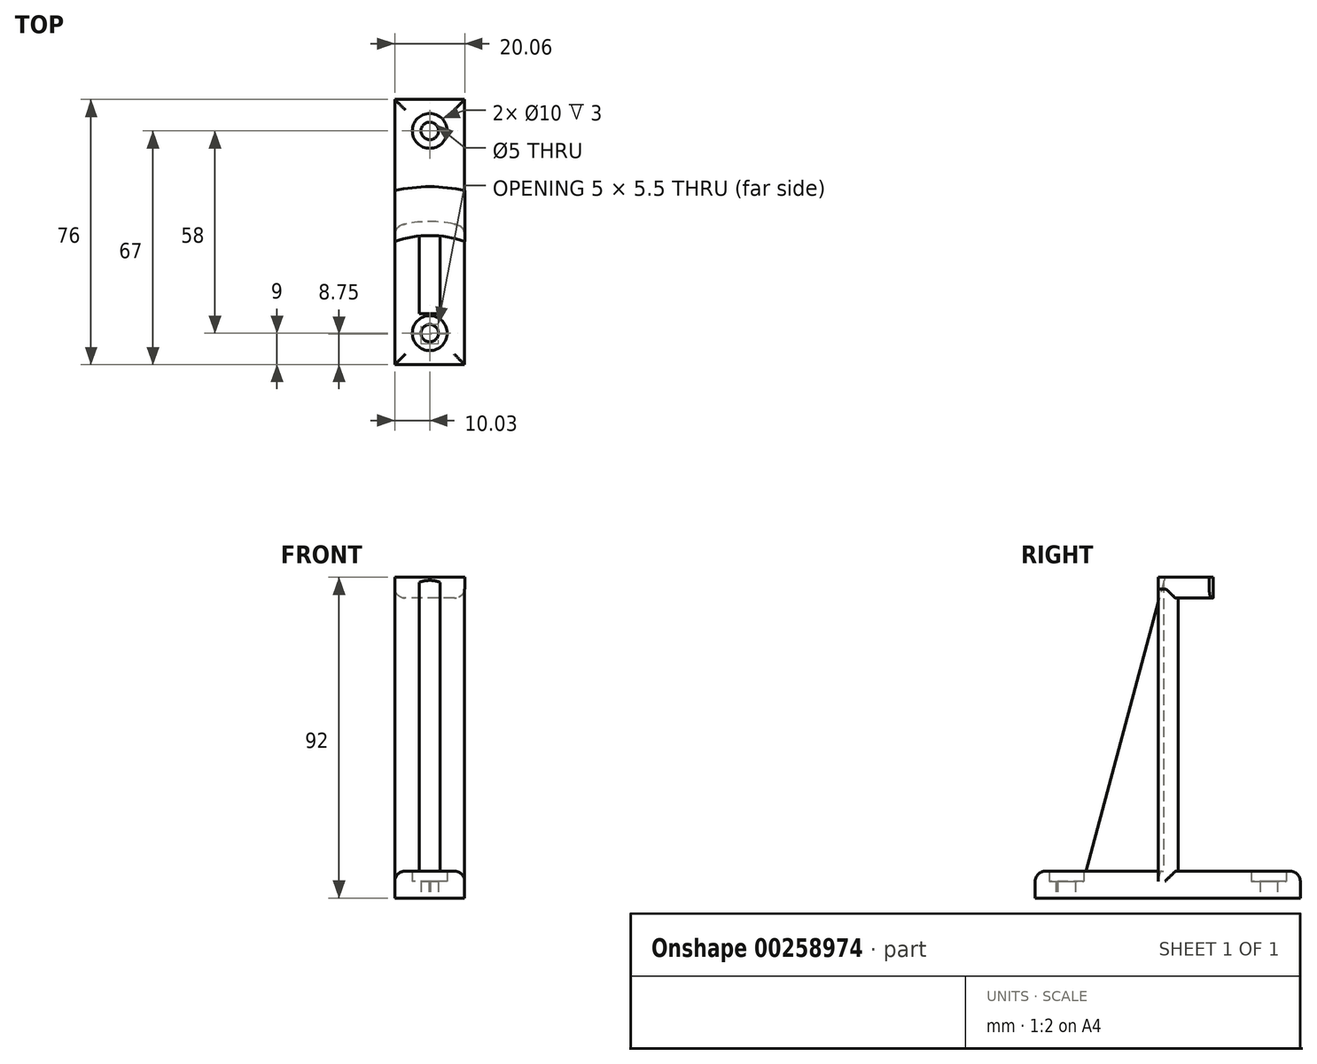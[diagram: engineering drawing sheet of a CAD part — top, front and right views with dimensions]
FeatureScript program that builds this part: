
annotation { "Feature Type Name" : "Feature", "Feature Type Description" : "" }
export const myFeature = defineFeature(function(context is Context, id is Id, definition is map)
    precondition{}
    {
        {
            var Q0;
            Q0=qCreatedBy(makeId("Top.planeOp"),FACE);
            var sketch = newSketch(context, id + "F0", { "sketchPlane" : qUnion([Q0])});
            skCircle(sketch, "E0", {"center": v(0, 0) * mm, "radius": 35 * mm});
            skCircle(sketch, "E1", {"center": v(0, 0) * mm, "radius": 31 * mm});
            skCircle(sketch, "E2", {"center": v(0, 0) * mm, "radius": 45 * mm});
            skLineSegment(sketch, "E3", {"start": v(0, 0) * mm, "end": v(-15.4, 42.29) * mm});
            skLineSegment(sketch, "E4", {"start": v(0, 0) * mm, "end": v(15.4, 42.29) * mm});
            skLineSegment(sketch, "E5", {"start": v(0, 0) * mm, "end": v(0, 45) * mm});
            skLineSegment(sketch, "E6.bottom", {"start": v(10, 35) * mm, "end": v(-10, 35) * mm});
            skLineSegment(sketch, "E6.top", {"start": v(10, 70) * mm, "end": v(-10, 70) * mm});
            skLineSegment(sketch, "E6.left", {"start": v(10, 35) * mm, "end": v(10, 70) * mm});
            skLineSegment(sketch, "E6.right", {"start": v(-10, 35) * mm, "end": v(-10, 70) * mm});
            skPoint(sketch, "E6.middle", {"position": v(0, 52.5) * mm});
            skCircle(sketch, "E7", {"center": v(0, 61) * mm, "radius": 5 * mm});
            skCircle(sketch, "E8", {"center": v(0, 61) * mm, "radius": 2.5 * mm});
            skLineSegment(sketch, "E9.bottom", {"start": v(10, -6) * mm, "end": v(-10, -6) * mm});
            skLineSegment(sketch, "E9.left", {"start": v(10, -6) * mm, "end": v(10, 35) * mm});
            skLineSegment(sketch, "E9.right", {"start": v(-10, -6) * mm, "end": v(-10, 35) * mm});
            skPoint(sketch, "E9.middle", {"position": v(0, 14.5) * mm});
            skCircle(sketch, "E10", {"center": v(0, 3) * mm, "radius": 2.5 * mm});
            skCircle(sketch, "E11", {"center": v(0, 3) * mm, "radius": 5 * mm});
            skSolve(sketch);
        }
        {
            var Q0;
            {var subQ0=sQuery(id+"F0.wireOp",EDGE,"E5");var subQ1=sQuery(id+"F0.wireOp",EDGE,"E0");var subQ2=makeQuery(id+"F0.imprint","INTERSECT",VERTEX,{"derivedFrom":[subQ1,subQ0]});Q0=makeQuery(id+"F0.imprint","IMPRINT",FACE,{"disambiguationData":[TD([[makeQuery(id+"F0.imprint","IMPRINT",EDGE,{"disambiguationData":[TD([[subQ2,1.0]])],"derivedFrom":subQ1}),1.0]])]});}
            var Q1;
            {var subQ0=sQuery(id+"F0.wireOp",EDGE,"E5");var subQ1=sQuery(id+"F0.wireOp",EDGE,"E0");var subQ2=makeQuery(id+"F0.imprint","INTERSECT",VERTEX,{"derivedFrom":[subQ1,subQ0]});Q1=makeQuery(id+"F0.imprint","IMPRINT",FACE,{"disambiguationData":[TD([[makeQuery(id+"F0.imprint","IMPRINT",EDGE,{"disambiguationData":[TD([[subQ2,-1.0]])],"derivedFrom":subQ1}),1.0]])]});}
            extrude(context, id + "F1", {"entities" : qUnion([Q0, Q1]), "depth" : 86 * mm});
        }
        {
            var Q0;
            {var subQ1=sQuery(id+"F0.wireOp",EDGE,"E6.top");Q0=makeQuery(id+"F0.imprint","IMPRINT",FACE,{"disambiguationData":[TD([[makeQuery(id+"F0.imprint","IMPRINT",EDGE,{"derivedFrom":subQ1}),1.0]])]});}
            var Q1;
            {var subQ0=sQuery(id+"F0.wireOp",EDGE,"E6.left");var subQ3=sQuery(id+"F0.wireOp",EDGE,"E2");var subQ4=makeQuery(id+"F0.imprint","INTERSECT",VERTEX,{"derivedFrom":[subQ3,subQ0]});Q1=makeQuery(id+"F0.imprint","IMPRINT",FACE,{"disambiguationData":[TD([[makeQuery(id+"F0.imprint","IMPRINT",EDGE,{"disambiguationData":[TD([[subQ4,-1.0]])],"derivedFrom":subQ3}),1.0]])]});}
            var Q2;
            {var subQ0=sQuery(id+"F0.wireOp",EDGE,"E6.right");var subQ7=sQuery(id+"F0.wireOp",EDGE,"E2");var subQ8=makeQuery(id+"F0.imprint","INTERSECT",VERTEX,{"derivedFrom":[subQ7,subQ0]});Q2=makeQuery(id+"F0.imprint","IMPRINT",FACE,{"disambiguationData":[TD([[makeQuery(id+"F0.imprint","IMPRINT",EDGE,{"disambiguationData":[TD([[subQ8,1.0]])],"derivedFrom":subQ7}),1.0]])]});}
            var Q3;
            {var subQ0=sQuery(id+"F0.wireOp",EDGE,"TI2dgXii-1qb5-BShp-2s3b-O6LjYehV9T6b");var subQ1=sQuery(id+"F0.wireOp",EDGE,"E0");var subQ2=makeQuery(id+"F0.imprint","INTERSECT",VERTEX,{"derivedFrom":[subQ1,subQ0]});Q3=makeQuery(id+"F0.imprint","IMPRINT",FACE,{"disambiguationData":[TD([[makeQuery(id+"F0.imprint","IMPRINT",EDGE,{"disambiguationData":[TD([[subQ2,-1.0]])],"derivedFrom":subQ1}),-1.0]])]});}
            var Q4;
            {var subQ0=sQuery(id+"F0.wireOp",EDGE,"7Phw61sN-cOW4-dQUR-ONVQ-3oVi0tRklzDX");var subQ1=sQuery(id+"F0.wireOp",EDGE,"E0");var subQ2=makeQuery(id+"F0.imprint","INTERSECT",VERTEX,{"derivedFrom":[subQ1,subQ0]});Q4=makeQuery(id+"F0.imprint","IMPRINT",FACE,{"disambiguationData":[TD([[makeQuery(id+"F0.imprint","IMPRINT",EDGE,{"disambiguationData":[TD([[subQ2,1.0]])],"derivedFrom":subQ1}),-1.0]])]});}
            var Q5;
            {var subQ0=sQuery(id+"F0.wireOp",EDGE,"E9.bottom");var subQ3=sQuery(id+"F0.wireOp",EDGE,"E9.left");var subQ5=makeQuery(id+"F0.imprint","INTERSECT",VERTEX,{"derivedFrom":[subQ0,subQ3]});Q5=makeQuery(id+"F0.imprint","IMPRINT",FACE,{"disambiguationData":[TD([[makeQuery(id+"F0.imprint","IMPRINT",EDGE,{"disambiguationData":[TD([[subQ5,-1.0]])],"derivedFrom":subQ3}),1.0]])]});}
            var Q6;
            {var subQ0=sQuery(id+"F0.wireOp",EDGE,"E9.bottom");var subQ3=sQuery(id+"F0.wireOp",EDGE,"E9.right");var subQ5=makeQuery(id+"F0.imprint","INTERSECT",VERTEX,{"derivedFrom":[subQ0,subQ3]});Q6=makeQuery(id+"F0.imprint","IMPRINT",FACE,{"disambiguationData":[TD([[makeQuery(id+"F0.imprint","IMPRINT",EDGE,{"disambiguationData":[TD([[subQ5,-1.0]])],"derivedFrom":subQ3}),-1.0]])]});}
            var Q7;
            {var subQ0=sQuery(id+"F0.wireOp",EDGE,"E5");var subQ1=sQuery(id+"F0.wireOp",EDGE,"E1");var subQ2=makeQuery(id+"F0.imprint","INTERSECT",VERTEX,{"derivedFrom":[subQ1,subQ0]});Q7=makeQuery(id+"F0.imprint","IMPRINT",FACE,{"disambiguationData":[TD([[makeQuery(id+"F0.imprint","IMPRINT",EDGE,{"disambiguationData":[TD([[subQ2,-1.0]])],"derivedFrom":subQ1}),1.0]])]});}
            var Q8;
            {var subQ0=sQuery(id+"F0.wireOp",EDGE,"E9.left");var subQ1=sQuery(id+"F0.wireOp",EDGE,"E1");var subQ2=makeQuery(id+"F0.imprint","INTERSECT",VERTEX,{"derivedFrom":[subQ1,subQ0]});Q8=makeQuery(id+"F0.imprint","IMPRINT",FACE,{"disambiguationData":[TD([[makeQuery(id+"F0.imprint","IMPRINT",EDGE,{"disambiguationData":[TD([[subQ2,-1.0]])],"derivedFrom":subQ1}),1.0]])]});}
            var Q9;
            {var subQ0=sQuery(id+"F0.wireOp",EDGE,"E9.left");var subQ1=sQuery(id+"F0.wireOp",EDGE,"E0");var subQ2=makeQuery(id+"F0.imprint","INTERSECT",VERTEX,{"derivedFrom":[subQ1,subQ0]});Q9=makeQuery(id+"F0.imprint","IMPRINT",FACE,{"disambiguationData":[TD([[makeQuery(id+"F0.imprint","IMPRINT",EDGE,{"disambiguationData":[TD([[subQ2,-1.0]])],"derivedFrom":subQ1}),-1.0]])]});}
            var Q10;
            {var subQ0=sQuery(id+"F0.wireOp",EDGE,"E9.right");var subQ1=sQuery(id+"F0.wireOp",EDGE,"E0");var subQ2=makeQuery(id+"F0.imprint","INTERSECT",VERTEX,{"derivedFrom":[subQ1,subQ0]});Q10=makeQuery(id+"F0.imprint","IMPRINT",FACE,{"disambiguationData":[TD([[makeQuery(id+"F0.imprint","IMPRINT",EDGE,{"disambiguationData":[TD([[subQ2,1.0]])],"derivedFrom":subQ1}),-1.0]])]});}
            extrude(context, id + "F2", {"entities" : qUnion([Q0, Q1, Q2, Q3, Q4, Q5, Q6, Q7, Q8, Q9, Q10]), "operationType" : NewBodyOperationType.ADD, "depth" : 7.75 * mm});
        }
        {
            var Q0;
            Q0=qCreatedBy(makeId("Top.planeOp"),FACE);
            cPlane(context, id + "F3", {"entities" : qUnion([Q0]), "cplaneType" : CPlaneType.OFFSET, "offset" : 83 * mm, "width" : 150 * mm, "height" : 150 * mm});
        }
        {
            var Q0;
            Q0=qCreatedBy(id+"F3.planeOp",FACE);
            var sketch = newSketch(context, id + "F4", { "sketchPlane" : qUnion([Q0])});
            skCircle(sketch, "E12", {"center": v(0, 0) * mm, "radius": 31 * mm});
            skCircle(sketch, "E13", {"center": v(0, 0) * mm, "radius": 35 * mm});
            skCircle(sketch, "E14", {"center": v(0, 0) * mm, "radius": 45 * mm});
            skLineSegment(sketch, "E15", {"start": v(0, 0) * mm, "end": v(0, 45) * mm});
            skLineSegment(sketch, "E16", {"start": v(0, 0) * mm, "end": v(-15.4, 42.29) * mm});
            skLineSegment(sketch, "E17", {"start": v(0, 0) * mm, "end": v(15.4, 42.29) * mm});
            skLineSegment(sketch, "E18", {"start": v(10.03, 27.55) * mm, "end": v(10.03, 33.53) * mm});
            skLineSegment(sketch, "E19.MirrorCS", {"start": v(-10.03, 27.55) * mm, "end": v(-10.03, 33.53) * mm});
            skLineSegment(sketch, "E20", {"start": v(10.03, 33.53) * mm, "end": v(10.03, 43.87) * mm});
            skLineSegment(sketch, "E21.MirrorCS", {"start": v(-10.03, 33.53) * mm, "end": v(-10.03, 43.87) * mm});
            skSolve(sketch);
        }
        {
            var Q0;
            {var subQ0=sQuery(id+"F4.wireOp",EDGE,"E15");var subQ1=sQuery(id+"F4.wireOp",EDGE,"E12");var subQ2=makeQuery(id+"F4.imprint","INTERSECT",VERTEX,{"derivedFrom":[subQ1,subQ0]});Q0=makeQuery(id+"F4.imprint","IMPRINT",FACE,{"disambiguationData":[TD([[makeQuery(id+"F4.imprint","IMPRINT",EDGE,{"disambiguationData":[TD([[subQ2,1.0]])],"derivedFrom":subQ1}),-1.0]])]});}
            var Q1;
            {var subQ0=sQuery(id+"F4.wireOp",EDGE,"E15");var subQ1=sQuery(id+"F4.wireOp",EDGE,"E12");var subQ2=makeQuery(id+"F4.imprint","INTERSECT",VERTEX,{"derivedFrom":[subQ1,subQ0]});Q1=makeQuery(id+"F4.imprint","IMPRINT",FACE,{"disambiguationData":[TD([[makeQuery(id+"F4.imprint","IMPRINT",EDGE,{"disambiguationData":[TD([[subQ2,-1.0]])],"derivedFrom":subQ1}),-1.0]])]});}
            var Q2;
            {var subQ0=sQuery(id+"F4.wireOp",EDGE,"E15");var subQ1=sQuery(id+"F4.wireOp",EDGE,"E13");var subQ2=makeQuery(id+"F4.imprint","INTERSECT",VERTEX,{"derivedFrom":[subQ1,subQ0]});Q2=makeQuery(id+"F4.imprint","IMPRINT",FACE,{"disambiguationData":[TD([[makeQuery(id+"F4.imprint","IMPRINT",EDGE,{"disambiguationData":[TD([[subQ2,1.0]])],"derivedFrom":subQ1}),-1.0]])]});}
            var Q3;
            {var subQ0=sQuery(id+"F4.wireOp",EDGE,"E15");var subQ1=sQuery(id+"F4.wireOp",EDGE,"E13");var subQ2=makeQuery(id+"F4.imprint","INTERSECT",VERTEX,{"derivedFrom":[subQ1,subQ0]});Q3=makeQuery(id+"F4.imprint","IMPRINT",FACE,{"disambiguationData":[TD([[makeQuery(id+"F4.imprint","IMPRINT",EDGE,{"disambiguationData":[TD([[subQ2,-1.0]])],"derivedFrom":subQ1}),-1.0]])]});}
            extrude(context, id + "F5", {"entities" : qUnion([Q0, Q1, Q2, Q3]), "operationType" : NewBodyOperationType.ADD, "depth" : 9 * mm, "hasSecondDirection" : true, "secondDirectionOppositeDirection" : false, "secondDirectionDepth" : 3 * mm});
        }
        {
            var Q0;
            {var subQ0=sQuery(id+"F0.wireOp",EDGE,"E5");var subQ1=sQuery(id+"F0.wireOp",EDGE,"E2");var subQ2=makeQuery(id+"F0.imprint","INTERSECT",VERTEX,{"derivedFrom":[subQ1,subQ0]});Q0=makeQuery(id+"F0.imprint","IMPRINT",FACE,{"disambiguationData":[TD([[makeQuery(id+"F0.imprint","IMPRINT",EDGE,{"disambiguationData":[TD([[subQ2,1.0]])],"derivedFrom":subQ1}),1.0]])]});}
            var Q1;
            {var subQ0=sQuery(id+"F0.wireOp",EDGE,"E5");var subQ1=sQuery(id+"F0.wireOp",EDGE,"E2");var subQ2=makeQuery(id+"F0.imprint","INTERSECT",VERTEX,{"derivedFrom":[subQ1,subQ0]});Q1=makeQuery(id+"F0.imprint","IMPRINT",FACE,{"disambiguationData":[TD([[makeQuery(id+"F0.imprint","IMPRINT",EDGE,{"disambiguationData":[TD([[subQ2,-1.0]])],"derivedFrom":subQ1}),1.0]])]});}
            var Q2;
            Q2=makeQuery(id+"F0.imprint","IMPRINT",FACE,{"disambiguationData":[TD([[makeQuery(id+"F0.imprint","IMPRINT",EDGE,{"derivedFrom":sQuery(id+"F0.wireOp",EDGE,"E7")}),1.0]])]});
            var Q3;
            {var subQ1=sQuery(id+"F0.wireOp",EDGE,"E6.top");Q3=makeQuery(id+"F0.imprint","IMPRINT",FACE,{"disambiguationData":[TD([[makeQuery(id+"F0.imprint","IMPRINT",EDGE,{"derivedFrom":subQ1}),1.0]])]});}
            var Q4;
            {var subQ0=sQuery(id+"F0.wireOp",EDGE,"E10");var subQ5=sQuery(id+"F0.wireOp",EDGE,"E3");var subQ9=makeQuery(id+"F0.imprint","INTERSECT",VERTEX,{"disambiguationData":[OD(1.0)],"derivedFrom":[subQ5,subQ0]});Q4=makeQuery(id+"F0.imprint","IMPRINT",FACE,{"disambiguationData":[TD([[makeQuery(id+"F0.imprint","IMPRINT",EDGE,{"disambiguationData":[TD([[subQ9,-1.0]])],"derivedFrom":subQ5}),1.0]])]});}
            var Q5;
            {var subQ0=sQuery(id+"F0.wireOp",EDGE,"E10");var subQ1=sQuery(id+"F0.wireOp",EDGE,"E3");var subQ2=makeQuery(id+"F0.imprint","INTERSECT",VERTEX,{"disambiguationData":[OD(1.0)],"derivedFrom":[subQ1,subQ0]});Q5=makeQuery(id+"F0.imprint","IMPRINT",FACE,{"disambiguationData":[TD([[makeQuery(id+"F0.imprint","IMPRINT",EDGE,{"disambiguationData":[TD([[subQ2,-1.0]])],"derivedFrom":subQ1}),-1.0]])]});}
            var Q6;
            {var subQ0=sQuery(id+"F0.wireOp",EDGE,"E10");var subQ1=sQuery(id+"F0.wireOp",EDGE,"E4");var subQ2=makeQuery(id+"F0.imprint","INTERSECT",VERTEX,{"disambiguationData":[OD(1.0)],"derivedFrom":[subQ1,subQ0]});Q6=makeQuery(id+"F0.imprint","IMPRINT",FACE,{"disambiguationData":[TD([[makeQuery(id+"F0.imprint","IMPRINT",EDGE,{"disambiguationData":[TD([[subQ2,-1.0]])],"derivedFrom":subQ1}),1.0]])]});}
            extrude(context, id + "F6", {"entities" : qUnion([Q0, Q1, Q2, Q3, Q4, Q5, Q6]), "operationType" : NewBodyOperationType.ADD, "depth" : 4.75 * mm});
        }
        {
            var Q0;
            Q0=qCreatedBy(makeId("Right.planeOp"),FACE);
            var sketch = newSketch(context, id + "F7", { "sketchPlane" : qUnion([Q0])});
            skLineSegment(sketch, "E22", {"start": v(8.63, 7.75) * mm, "end": v(31.18, 7.75) * mm});
            skLineSegment(sketch, "E23", {"start": v(31.18, 7.75) * mm, "end": v(31.18, 91.75) * mm});
            skLineSegment(sketch, "E24", {"start": v(31.18, 91.75) * mm, "end": v(8.63, 7.75) * mm});
            skSolve(sketch);
        }
        {
            var Q0;
            Q0=makeQuery(id+"F7.imprint","IMPRINT",FACE,{"disambiguationData":[TD([[makeQuery(id+"F7.imprint","IMPRINT",EDGE,{"derivedFrom":sQuery(id+"F7.wireOp",EDGE,"E22")}),1.0]])]});
            extrude(context, id + "F8", {"entities" : qUnion([Q0]), "operationType" : NewBodyOperationType.ADD, "depth" : 3 * mm, "hasSecondDirection" : true, "secondDirectionOppositeDirection" : true, "secondDirectionDepth" : 3 * mm});
        }
        {
            var Q0;
            Q0=makeQuery(id+"F5.opExtrude","CAP_EDGE",EDGE,{"disambiguationData":[OSD([sQuery(id+"F4.wireOp",EDGE,"E19.MirrorCS"),sQuery(id+"F4.wireOp",EDGE,"E21.MirrorCS")])],"isStart":true});
            var Q1;
            Q1=makeQuery(id+"F5.opExtrude","CAP_EDGE",EDGE,{"disambiguationData":[OSD([sQuery(id+"F4.wireOp",EDGE,"E18"),sQuery(id+"F4.wireOp",EDGE,"E20")])],"isStart":true});
            var Q2;
            Q2=makeQuery(id+"F2.opExtrude","CAP_EDGE",EDGE,{"disambiguationData":[OSD([sQuery(id+"F0.wireOp",EDGE,"E6.left"),sQuery(id+"F0.wireOp",EDGE,"E9.left")])],"isStart":false});
            var Q3;
            Q3=makeQuery(id+"F2.opExtrude","CAP_EDGE",EDGE,{"disambiguationData":[OSD([sQuery(id+"F0.wireOp",EDGE,"E6.right"),sQuery(id+"F0.wireOp",EDGE,"E9.right")])],"isStart":false});
            var Q4;
            Q4=makeQuery(id+"F2.opExtrude","CAP_EDGE",EDGE,{"disambiguationData":[OSD([sQuery(id+"F0.wireOp",EDGE,"E9.right")])],"isStart":false});
            var Q5;
            Q5=makeQuery(id+"F2.opExtrude","CAP_EDGE",EDGE,{"disambiguationData":[OSD([sQuery(id+"F0.wireOp",EDGE,"E9.left")])],"isStart":false});
            var Q6;
            Q6=makeQuery(id+"F2.opExtrude","CAP_EDGE",EDGE,{"disambiguationData":[OSD([sQuery(id+"F0.wireOp",EDGE,"E6.top")])],"isStart":false});
            var Q7;
            Q7=makeQuery(id+"F2.opExtrude","CAP_EDGE",EDGE,{"disambiguationData":[OSD([sQuery(id+"F0.wireOp",EDGE,"E9.bottom")])],"isStart":false});
            fillet(context, id + "F9", {"entities" : qUnion([Q0, Q1, Q2, Q3, Q4, Q5, Q6, Q7]), "radius" : 3 * mm, "tangentPropagation" : true, "allowEdgeOverflow" : false});
        }
        {
            var Q0;
            Q0=makeQuery(id+"F1.opExtrude","SWEPT_EDGE",EDGE,{"disambiguationData":[OSD([sQuery(id+"F0.wireOp",EDGE,"E0"),sQuery(id+"F0.wireOp",EDGE,"E9.left")])]});
            var Q1;
            Q1=makeQuery(id+"F1.opExtrude","SWEPT_EDGE",EDGE,{"disambiguationData":[OSD([sQuery(id+"F0.wireOp",EDGE,"E0"),sQuery(id+"F0.wireOp",EDGE,"E9.right")])]});
            fillet(context, id + "F10", {"entities" : qUnion([Q0, Q1]), "radius" : 3 * mm, "tangentPropagation" : true, "allowEdgeOverflow" : false});
        }
    });
